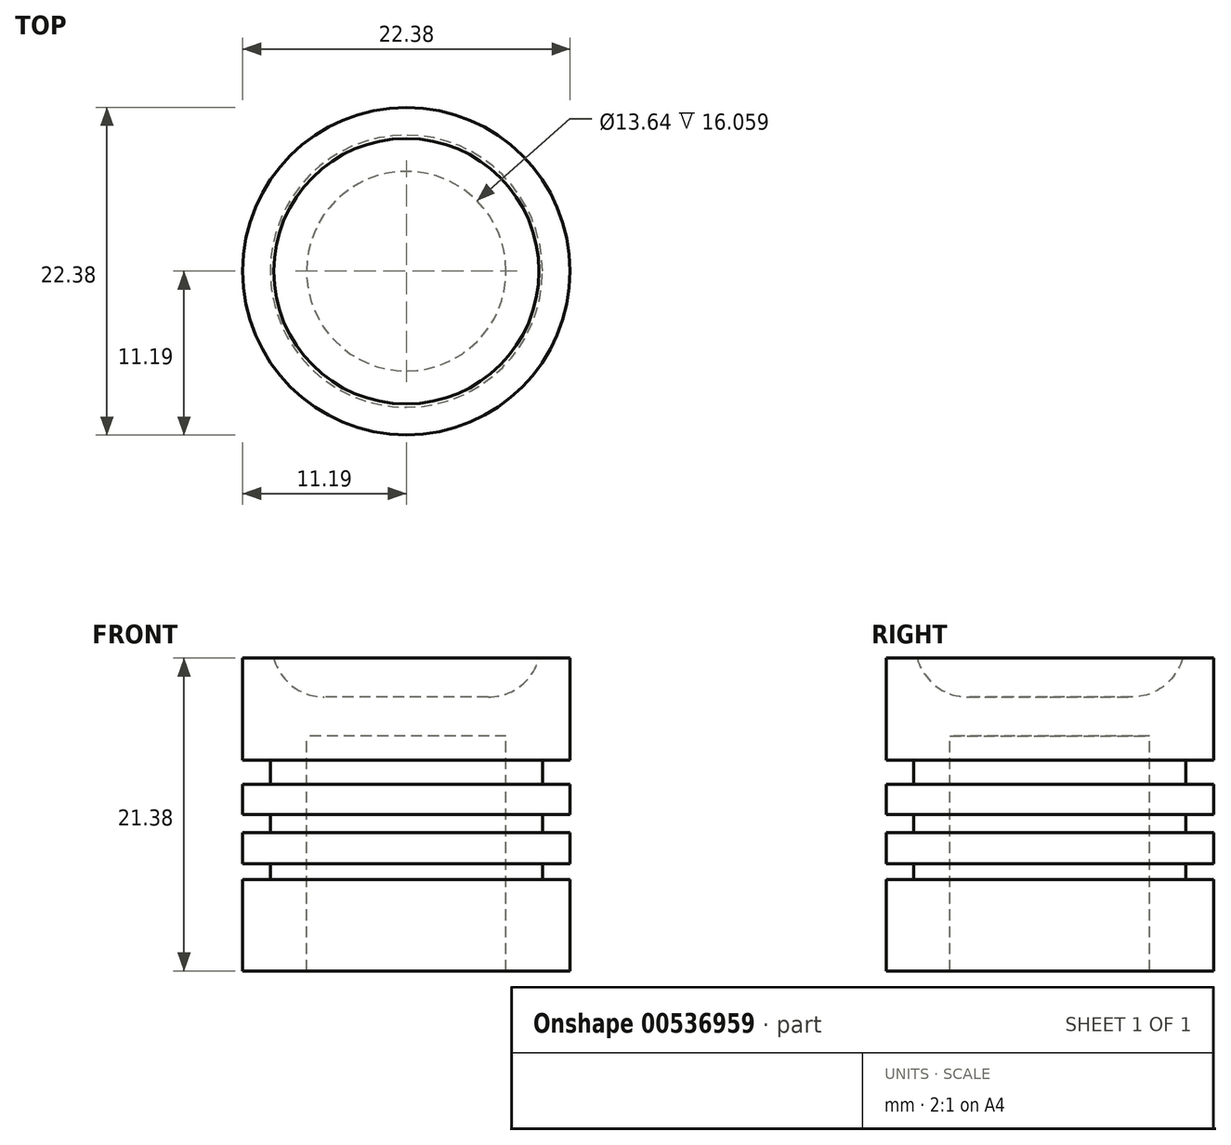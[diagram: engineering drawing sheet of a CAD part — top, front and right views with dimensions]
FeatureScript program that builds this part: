
annotation { "Feature Type Name" : "Feature", "Feature Type Description" : "" }
export const myFeature = defineFeature(function(context is Context, id is Id, definition is map)
    precondition{}
    {
        {
            var Q0;
            Q0=qCreatedBy(makeId("Front.planeOp"),FACE);
            var sketch = newSketch(context, id + "F0", { "sketchPlane" : qUnion([Q0])});
            skLineSegment(sketch, "E0", {"start": v(0, 16.06) * mm, "end": v(-6.82, 16.06) * mm});
            skLineSegment(sketch, "E1", {"start": v(-6.82, 16.06) * mm, "end": v(-6.82, 0) * mm});
            skLineSegment(sketch, "E2", {"start": v(-6.82, 0) * mm, "end": v(-11.2, 0) * mm});
            skLineSegment(sketch, "E3", {"start": v(-11.2, 0) * mm, "end": v(-11.2, 6.25) * mm});
            skLineSegment(sketch, "E4", {"start": v(-11.2, 21.38) * mm, "end": v(-9.07, 21.38) * mm});
            skLineSegment(sketch, "E5", {"start": v(0, 18.72) * mm, "end": v(0, 16.06) * mm});
            skPoint(sketch, "E6.start.orphan", {"position": v(0, 18.72) * mm});
            skLineSegment(sketch, "E7", {"start": v(0, 18.72) * mm, "end": v(-5.6, 18.72) * mm});
            skPoint(sketch, "E7.endSnap0", {"position": v(-5.6, 21.38) * mm});
            skArc(sketch, "E8", {"start": v(-9.07, 21.38) * mm, "mid": v(-7.78, 19.46) * mm, "end": v(-5.6, 18.72) * mm});
            skPoint(sketch, "E9.orphan", {"position": v(0, 21.38) * mm});
            skLineSegment(sketch, "E10", {"start": v(-11.2, 14.4) * mm, "end": v(-9.3, 14.4) * mm});
            skLineSegment(sketch, "E11", {"start": v(-9.3, 14.4) * mm, "end": v(-9.3, 12.75) * mm});
            skLineSegment(sketch, "E12", {"start": v(-9.3, 12.75) * mm, "end": v(-11.2, 12.75) * mm});
            skLineSegment(sketch, "E13", {"start": v(-11.2, 10.69) * mm, "end": v(-9.3, 10.69) * mm});
            skLineSegment(sketch, "E14", {"start": v(-9.3, 10.69) * mm, "end": v(-9.3, 9.44) * mm});
            skLineSegment(sketch, "E15", {"start": v(-9.3, 9.44) * mm, "end": v(-11.2, 9.44) * mm});
            skLineSegment(sketch, "E16", {"start": v(-11.2, 7.32) * mm, "end": v(-9.3, 7.32) * mm});
            skLineSegment(sketch, "E17", {"start": v(-9.3, 7.32) * mm, "end": v(-9.3, 6.25) * mm});
            skLineSegment(sketch, "E18", {"start": v(-9.3, 6.25) * mm, "end": v(-11.2, 6.25) * mm});
            skLineSegment(sketch, "E19.trimOffspring", {"start": v(-11.2, 14.4) * mm, "end": v(-11.2, 21.38) * mm});
            skLineSegment(sketch, "E20.trimOffspring", {"start": v(-11.2, 10.69) * mm, "end": v(-11.2, 12.75) * mm});
            skLineSegment(sketch, "E21.trimOffspring", {"start": v(-11.2, 7.32) * mm, "end": v(-11.2, 9.44) * mm});
            skSolve(sketch);
        }
        {
            var Q0;
            Q0 = qSketchRegion(id + "F0", true);
            var Q1;
            Q1=sQuery(id+"F0.wireOp",EDGE,"E5");
            revolve(context, id + "F1", {"entities" : qUnion([Q0]), "axis" : qUnion([Q1]), "revolveType" : RevolveType.FULL});
        }
    });
